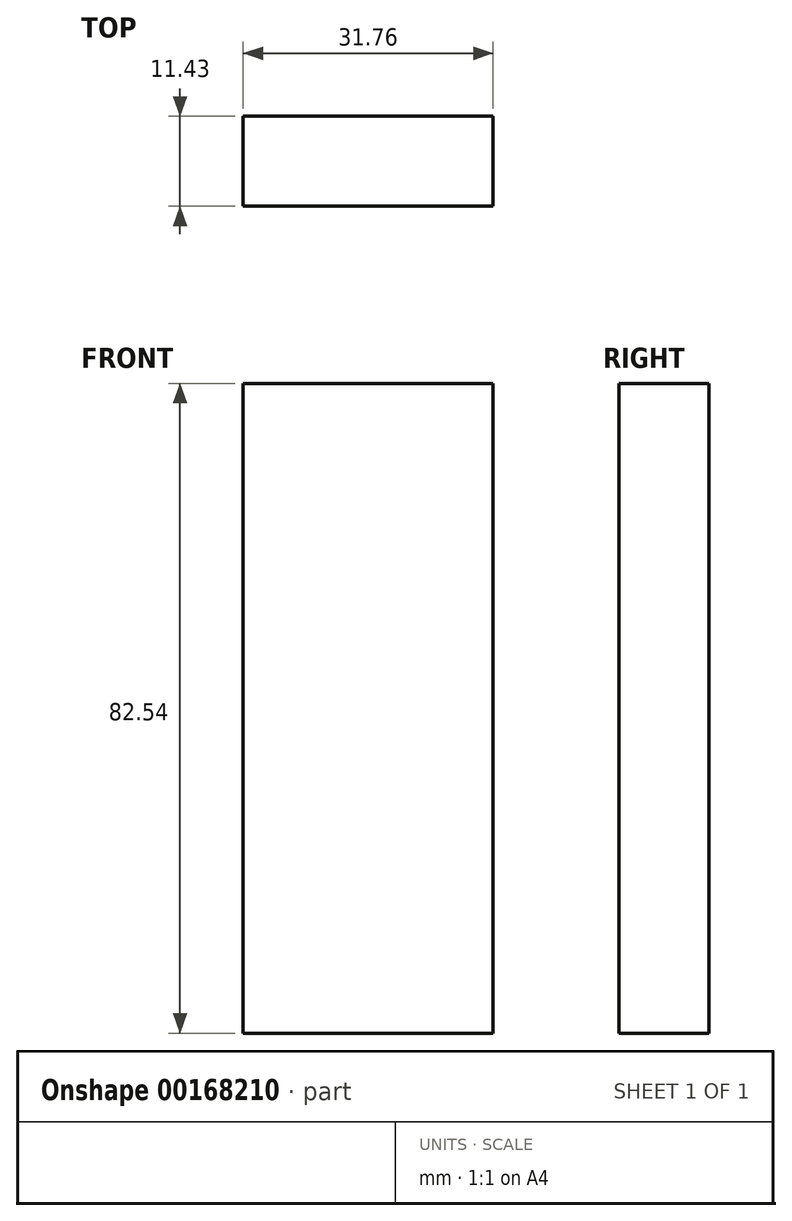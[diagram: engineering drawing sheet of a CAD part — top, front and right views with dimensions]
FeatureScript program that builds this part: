
annotation { "Feature Type Name" : "Feature", "Feature Type Description" : "" }
export const myFeature = defineFeature(function(context is Context, id is Id, definition is map)
    precondition{}
    {
        {
            var Q0;
            Q0=qCreatedBy(makeId("Front.planeOp"),FACE);
            var sketch = newSketch(context, id + "F0", { "sketchPlane" : qUnion([Q0])});
            skLineSegment(sketch, "E0.bottom", {"start": v(15.88, -41.28) * mm, "end": v(-15.87, -41.28) * mm});
            skLineSegment(sketch, "E0.top", {"start": v(15.87, 41.28) * mm, "end": v(-15.88, 41.28) * mm});
            skLineSegment(sketch, "E0.left", {"start": v(15.88, -41.28) * mm, "end": v(15.87, 41.28) * mm});
            skLineSegment(sketch, "E0.right", {"start": v(-15.87, -41.28) * mm, "end": v(-15.88, 41.28) * mm});
            skPoint(sketch, "E0.middle", {"position": v(0, 0) * mm});
            skSolve(sketch);
        }
        {
            var Q0;
            Q0=qSketchRegion(id+"F0",true);
            extrude(context, id + "F1", {"entities" : qUnion([Q0]), "depth" : 11.43 * mm});
        }
    });
